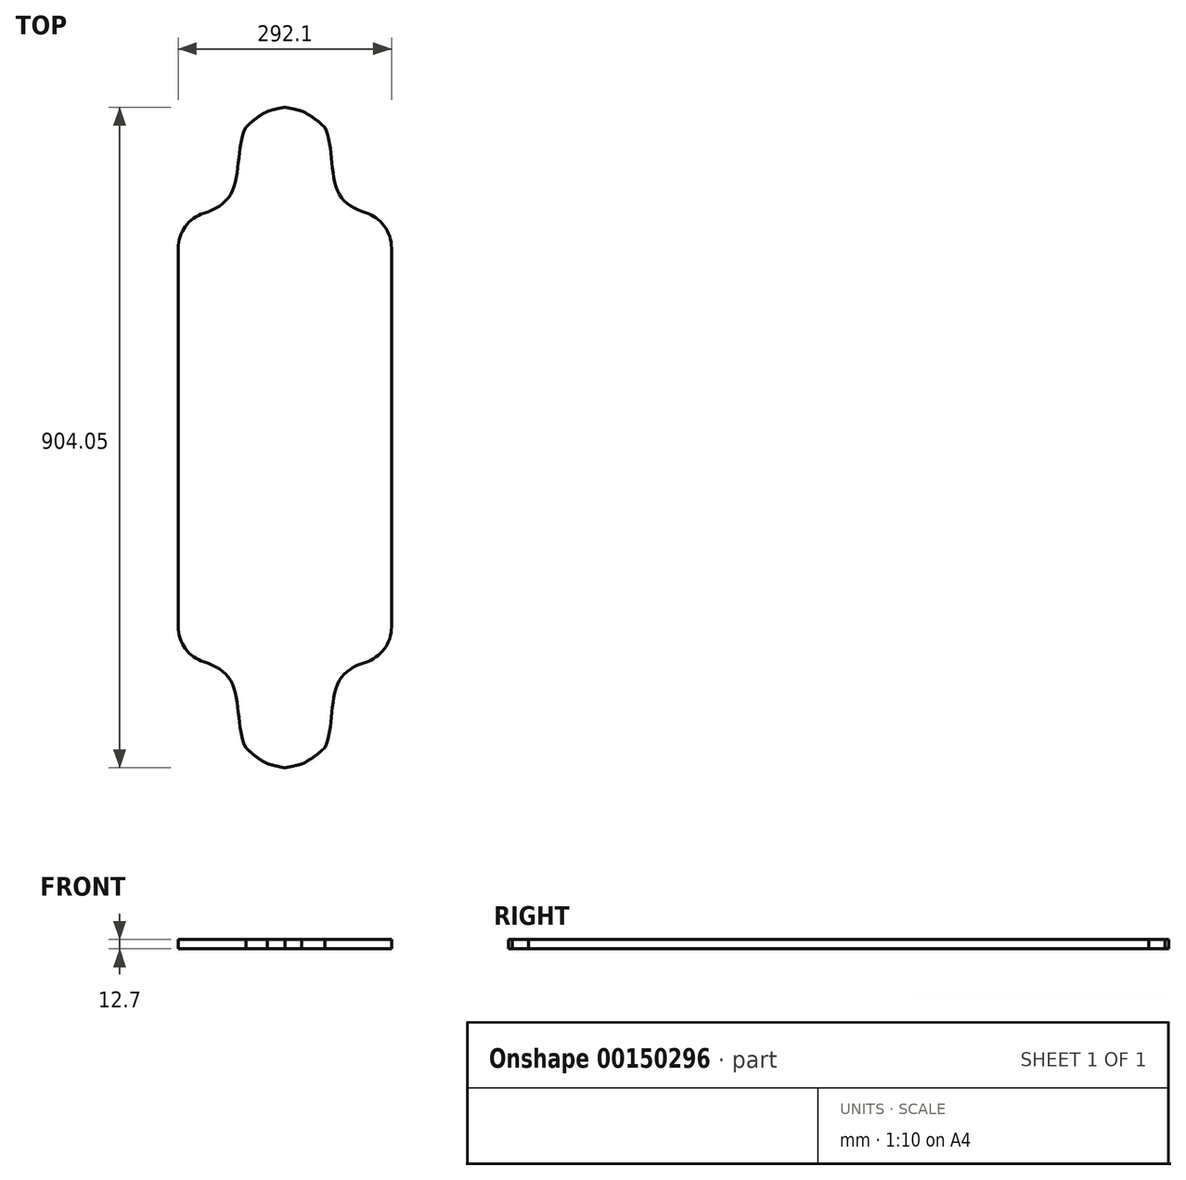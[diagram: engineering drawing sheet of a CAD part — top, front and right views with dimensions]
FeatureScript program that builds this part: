
annotation { "Feature Type Name" : "Feature", "Feature Type Description" : "" }
export const myFeature = defineFeature(function(context is Context, id is Id, definition is map)
    precondition{}
    {
        {
            var Q0;
            Q0=qCreatedBy(makeId("Top.planeOp"),FACE);
            var sketch = newSketch(context, id + "F0", { "sketchPlane" : qUnion([Q0])});
            skLineSegment(sketch, "E0", {"start": v(-146.05, 268.28) * mm, "end": v(-146.05, 9.59) * mm});
            skLineSegment(sketch, "E1", {"start": v(146.05, 268.76) * mm, "end": v(146.05, 9.59) * mm});
            skPoint(sketch, "E2", {"position": v(0, 309.21) * mm});
            skPoint(sketch, "E3", {"position": v(0, 461.61) * mm});
            skFitSpline(sketch, "E4", {"points": [v(-146.05, 309.21) * mm, v(0, 461.61) * mm, v(146.05, 309.21) * mm], "startDerivative": vector(304.65, 455.86) * mm, "endDerivative": vector(279.48, -458.61) * mm});
            skFitSpline(sketch, "E5", {"points": [v(-146.05, 309.21) * mm, v(-74.15, 342.44) * mm, v(-53.33, 434.23) * mm, v(0, 461.61) * mm], "startDerivative": vector(263.83, 40.94) * mm, "endDerivative": vector(221.42, 45.73) * mm});
            skLineSegment(sketch, "E6", {"start": v(-74.15, 342.44) * mm, "end": v(0, 342.44) * mm, "construction": true});
            skLineSegment(sketch, "E7", {"start": v(0, 342.44) * mm, "end": v(74.53, 342.44) * mm, "construction": true});
            skLineSegment(sketch, "E8", {"start": v(74.53, 342.44) * mm, "end": v(77.26, 325.62) * mm, "construction": true});
            skLineSegment(sketch, "E9", {"start": v(-53.33, 434.23) * mm, "end": v(54.65, 434.23) * mm, "construction": true});
            skLineSegment(sketch, "E10", {"start": v(0, 342.44) * mm, "end": v(0, 309.21) * mm, "construction": true});
            skLineSegment(sketch, "E11", {"start": v(-146.05, 309.21) * mm, "end": v(-74.15, 309.21) * mm, "construction": true});
            skLineSegment(sketch, "E12", {"start": v(-74.15, 309.21) * mm, "end": v(-74.15, 9.59) * mm, "construction": true});
            skLineSegment(sketch, "E13", {"start": v(0, 434.23) * mm, "end": v(0, 309.21) * mm, "construction": true});
            skLineSegment(sketch, "E14", {"start": v(-53.33, 434.23) * mm, "end": v(0, 434.23) * mm, "construction": true});
            skLineSegment(sketch, "E15", {"start": v(54.65, 434.23) * mm, "end": v(54.65, 9.59) * mm, "construction": true});
            skFitSpline(sketch, "E16", {"points": [v(146.05, 309.21) * mm, v(74.53, 342.44) * mm, v(54.65, 434.23) * mm, v(0, 461.61) * mm], "startDerivative": vector(-262.66, 48.53) * mm, "endDerivative": vector(-225.77, 45.03) * mm});
            skLineSegment(sketch, "E17", {"start": v(74.53, 342.44) * mm, "end": v(74.53, 9.59) * mm, "construction": true});
            skArc(sketch, "E18.filletArc", {"start": v(-110.48, 316.74) * mm, "mid": v(-136.2, 298.33) * mm, "end": v(-146.05, 268.28) * mm});
            skArc(sketch, "E19.filletArc", {"start": v(146.05, 268.76) * mm, "mid": v(136.21, 298.8) * mm, "end": v(110.52, 317.22) * mm});
            skLineSegment(sketch, "E20.0", {"start": v(-146.05, 9.59) * mm, "end": v(146.05, 9.59) * mm, "construction": true});
            skLineSegment(sketch, "E21.MirrorCS", {"start": v(0, -323.26) * mm, "end": v(0, -290.04) * mm, "construction": true});
            skPoint(sketch, "E22.MirrorP", {"position": v(0, -290.04) * mm});
            skArc(sketch, "E23.MirrorCS", {"start": v(-110.48, -297.56) * mm, "mid": v(-136.2, -279.16) * mm, "end": v(-146.05, -249.1) * mm});
            skPoint(sketch, "E24.MirrorP", {"position": v(146.05, -290.04) * mm});
            skPoint(sketch, "E25.MirrorP", {"position": v(0, -442.44) * mm});
            skFitSpline(sketch, "E26.MirrorCS", {"points": [v(-146.05, -290.04) * mm, v(0, -442.44) * mm, v(146.05, -290.04) * mm], "startDerivative": vector(304.65, -455.86) * mm, "endDerivative": vector(279.48, 458.61) * mm});
            skLineSegment(sketch, "E27.MirrorCS", {"start": v(0, -323.26) * mm, "end": v(74.53, -323.26) * mm, "construction": true});
            skArc(sketch, "E28.MirrorCS", {"start": v(146.05, -249.59) * mm, "mid": v(136.21, -279.63) * mm, "end": v(110.52, -298.04) * mm});
            skFitSpline(sketch, "E29.MirrorCS", {"points": [v(146.05, -290.04) * mm, v(74.53, -323.26) * mm, v(54.65, -415.05) * mm, v(0, -442.44) * mm], "startDerivative": vector(-262.66, -48.53) * mm, "endDerivative": vector(-225.77, -45.03) * mm});
            skFitSpline(sketch, "E30.MirrorCS", {"points": [v(-146.05, -290.04) * mm, v(-74.15, -323.26) * mm, v(-53.33, -415.05) * mm, v(0, -442.44) * mm], "startDerivative": vector(263.83, -40.94) * mm, "endDerivative": vector(221.42, -45.73) * mm});
            skLineSegment(sketch, "E31.MirrorCS", {"start": v(-146.05, -290.04) * mm, "end": v(-74.15, -290.04) * mm, "construction": true});
            skLineSegment(sketch, "E32.MirrorCS", {"start": v(-53.33, -415.05) * mm, "end": v(0, -415.05) * mm, "construction": true});
            skLineSegment(sketch, "E33.MirrorCS", {"start": v(-53.33, -415.05) * mm, "end": v(54.65, -415.05) * mm, "construction": true});
            skLineSegment(sketch, "E34.MirrorCS", {"start": v(74.53, -323.26) * mm, "end": v(77.26, -306.44) * mm, "construction": true});
            skLineSegment(sketch, "E35.MirrorCS", {"start": v(-74.15, -323.26) * mm, "end": v(0, -323.26) * mm, "construction": true});
            skLineSegment(sketch, "E36.MirrorCS", {"start": v(0, -415.05) * mm, "end": v(0, -290.04) * mm, "construction": true});
            skLineSegment(sketch, "E37.MirrorCS", {"start": v(74.53, -323.26) * mm, "end": v(74.53, 9.59) * mm, "construction": true});
            skLineSegment(sketch, "E38.MirrorCS", {"start": v(-146.05, -249.1) * mm, "end": v(-146.05, 9.59) * mm});
            skFitSpline(sketch, "E39.MirrorCS", {"points": [v(146.05, -290.04) * mm, v(74.53, -323.26) * mm, v(54.65, -415.05) * mm, v(0, -442.44) * mm], "startDerivative": vector(-262.66, -48.53) * mm, "endDerivative": vector(-225.77, -45.03) * mm});
            skLineSegment(sketch, "E40.MirrorCS", {"start": v(54.65, -415.05) * mm, "end": v(54.65, 9.59) * mm, "construction": true});
            skLineSegment(sketch, "E41.MirrorCS", {"start": v(146.05, -249.59) * mm, "end": v(146.05, 9.59) * mm});
            skLineSegment(sketch, "E42.MirrorCS", {"start": v(-74.15, -290.04) * mm, "end": v(-74.15, 9.59) * mm, "construction": true});
            skSolve(sketch);
        }
        {
            var Q0;
            Q0=makeQuery(id+"F0.imprint","IMPRINT",FACE,{"disambiguationData":[TD([[makeQuery(id+"F0.imprint","IMPRINT",EDGE,{"derivedFrom":sQuery(id+"F0.wireOp",EDGE,"E0")}),1.0]])]});
            extrude(context, id + "F1", {"entities" : qUnion([Q0]), "depth" : 12.7 * mm});
        }
    });
